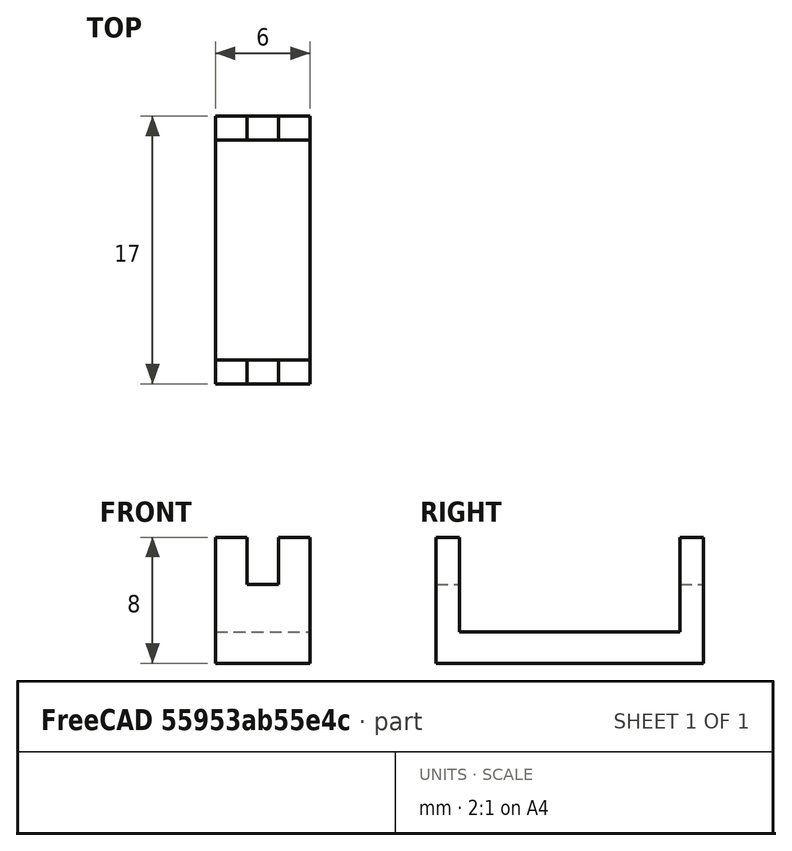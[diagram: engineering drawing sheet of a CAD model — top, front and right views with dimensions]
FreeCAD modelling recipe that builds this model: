
FCSTD DOCUMENT  (FreeCAD 0.19R24276 (Git))
Label: wheelJig
License: All rights reserved
LicenseURL: http://en.wikipedia.org/wiki/All_rights_reserved
objects: Part::Box×3, Part::Cut×2, Spreadsheet::Sheet×1
note: 5 computed .brp shape members not serialized (recipe doc carries the construction recipe); baked Part::Feature solids carry a one-line shape summary decoded from their .brp

FEATURE [Part::Box] Box  label="Cube"
  AttacherType = Attacher::AttachEngine3D
  Height = 8
  Length = 6
  Width = 17
  expr: Width = <<data>>.axle_width
  expr: Length = 6mm
  expr: .Placement.Base.x = 0mm
  expr: Height = <<data>>.outter_height
FEATURE [Spreadsheet::Sheet] Spreadsheet  label="data"
  cells = A5=axle_width; B5(axle_width)==17mm; A12=thickness; B12(thickness)==1.5mm; A13=outter_height; B13(outter_height)==8mm; A14=offset; B14(offset)==3mm
FEATURE [Part::Box] Box009  label="Cube001"
  AttacherType = Attacher::AttachEngine3D
  Height = 9
  Length = 6
  Placement = pos=(0,1.5,2) rot=(0,0,1;0rad)
  Width = 14
  expr: .Placement.Base.y = <<data>>.thickness
  expr: Length = 6mm
  expr: Width = <<data>>.axle_width - 2 * <<data>>.thickness
  expr: Height = <<data>>.outter_height + 1mm
FEATURE [Part::Box] Box010  label="Cube002"
  AttacherType = Attacher::AttachEngine3D
  Height = 8
  Length = 2
  Placement = pos=(2,0,5) rot=(0,0,1;0rad)
  Width = 17
  expr: Length = 2mm
  expr: Width = <<data>>.axle_width
  expr: Height = <<data>>.outter_height
  expr: .Placement.Base.z = <<data>>.outter_height - <<data>>.offset
FEATURE [Part::Cut] Cut
  Base = -> Box
  Tool = -> Box009
FEATURE [Part::Cut] Cut001
  Base = -> Cut
  Tool = -> Box010
